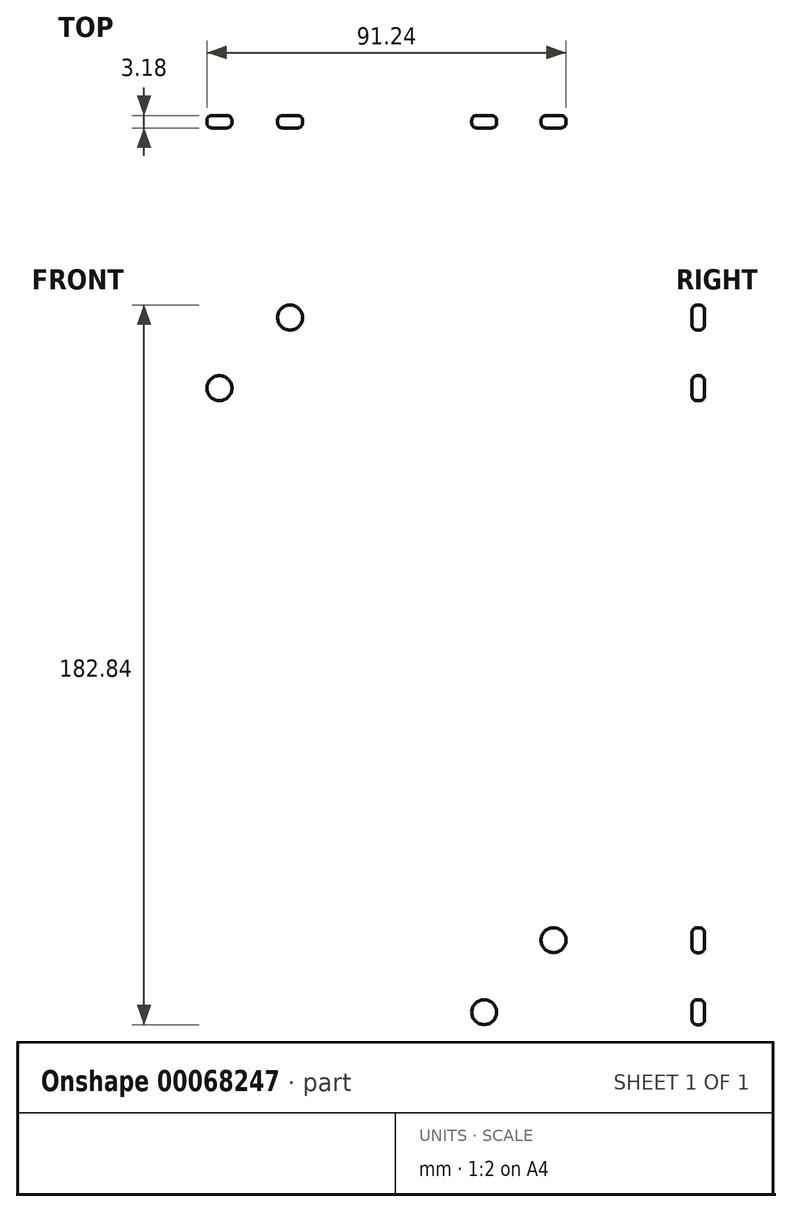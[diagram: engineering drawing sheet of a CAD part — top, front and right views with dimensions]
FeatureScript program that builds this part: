
annotation { "Feature Type Name" : "Feature", "Feature Type Description" : "" }
export const myFeature = defineFeature(function(context is Context, id is Id, definition is map)
    precondition{}
    {
        {
            var Q0;
            Q0=qCreatedBy(makeId("Front.planeOp"),FACE);
            var sketch = newSketch(context, id + "F0", { "sketchPlane" : qUnion([Q0])});
            skLineSegment(sketch, "E0.bottom", {"start": v(-302.85, 118.42) * mm, "end": v(509.95, 118.42) * mm});
            skLineSegment(sketch, "E0.top", {"start": v(-302.85, -103.83) * mm, "end": v(509.95, -103.83) * mm});
            skLineSegment(sketch, "E0.left", {"start": v(-302.85, 118.42) * mm, "end": v(-302.85, -103.83) * mm});
            skLineSegment(sketch, "E0.right", {"start": v(509.95, 118.42) * mm, "end": v(509.95, -103.83) * mm});
            skLineSegment(sketch, "E1", {"start": v(103.55, 118.42) * mm, "end": v(103.55, -103.83) * mm, "construction": true});
            skLineSegment(sketch, "E2", {"start": v(103.55, -103.83) * mm, "end": v(509.95, 7.3) * mm, "construction": true});
            skLineSegment(sketch, "E3", {"start": v(509.95, 7.3) * mm, "end": v(-302.85, 7.3) * mm, "construction": true});
            skLineSegment(sketch, "E4", {"start": v(-302.85, 7.3) * mm, "end": v(103.55, 118.42) * mm, "construction": true});
            skLineSegment(sketch, "E5", {"start": v(509.95, 7.3) * mm, "end": v(103.55, 118.42) * mm, "construction": true});
            skLineSegment(sketch, "E6", {"start": v(-302.85, 7.3) * mm, "end": v(103.55, -103.83) * mm, "construction": true});
            skCircle(sketch, "E7", {"center": v(52.75, 7.3) * mm, "radius": 25.4 * mm});
            skCircle(sketch, "E8", {"center": v(154.35, 7.3) * mm, "radius": 25.4 * mm});
            skLineSegment(sketch, "E9", {"start": v(52.75, 32.7) * mm, "end": v(154.35, 32.7) * mm});
            skLineSegment(sketch, "E10", {"start": v(52.75, -18.1) * mm, "end": v(154.35, -18.1) * mm});
            skLineSegment(sketch, "E11", {"start": v(103.55, 32.7) * mm, "end": v(103.55, 0) * mm, "construction": true});
            skCircle(sketch, "E12", {"center": v(79.74, -60.97) * mm, "radius": 4.76 * mm});
            skCircle(sketch, "E13", {"center": v(127.37, -60.97) * mm, "radius": 4.76 * mm});
            skLineSegment(sketch, "E14", {"start": v(79.74, -56.2) * mm, "end": v(127.37, -56.2) * mm});
            skLineSegment(sketch, "E15", {"start": v(127.37, -65.73) * mm, "end": v(79.74, -65.73) * mm});
            skLineSegment(sketch, "E16", {"start": v(103.55, -78.7) * mm, "end": v(103.55, -62.77) * mm, "construction": true});
            skPoint(sketch, "E16.startSnap0", {"position": v(103.55, -65.73) * mm});
            skLineSegment(sketch, "E17", {"start": v(79.74, 67.62) * mm, "end": v(127.37, 67.62) * mm});
            skLineSegment(sketch, "E18", {"start": v(127.37, 58.1) * mm, "end": v(79.74, 58.1) * mm});
            skCircle(sketch, "E19", {"center": v(127.37, 62.85) * mm, "radius": 4.76 * mm});
            skCircle(sketch, "E20", {"center": v(79.74, 62.85) * mm, "radius": 4.76 * mm});
            skLineSegment(sketch, "E21", {"start": v(103.55, 58.1) * mm, "end": v(103.55, 67.62) * mm, "construction": true});
            skLineSegment(sketch, "E22.1.0.0", {"start": v(19.4, -65.73) * mm, "end": v(-28.22, -65.73) * mm});
            skLineSegment(sketch, "E22.1.0.1", {"start": v(-28.22, -56.2) * mm, "end": v(19.4, -56.2) * mm});
            skCircle(sketch, "E22.1.0.2", {"center": v(19.4, -60.97) * mm, "radius": 4.76 * mm});
            skCircle(sketch, "E22.1.0.3", {"center": v(-28.22, -60.97) * mm, "radius": 4.76 * mm});
            skLineSegment(sketch, "E22.2.0.0", {"start": v(-88.56, -65.73) * mm, "end": v(-136.18, -65.73) * mm});
            skLineSegment(sketch, "E22.2.0.1", {"start": v(-136.18, -56.2) * mm, "end": v(-88.56, -56.2) * mm});
            skCircle(sketch, "E22.2.0.2", {"center": v(-88.56, -60.97) * mm, "radius": 4.76 * mm});
            skCircle(sketch, "E22.2.0.3", {"center": v(-136.18, -60.97) * mm, "radius": 4.76 * mm});
            skLineSegment(sketch, "E22.3.0.0", {"start": v(-196.52, -65.73) * mm, "end": v(-244.14, -65.73) * mm});
            skLineSegment(sketch, "E22.3.0.1", {"start": v(-244.14, -56.2) * mm, "end": v(-196.52, -56.2) * mm});
            skCircle(sketch, "E22.3.0.2", {"center": v(-196.52, -60.97) * mm, "radius": 4.76 * mm});
            skCircle(sketch, "E22.3.0.3", {"center": v(-244.14, -60.97) * mm, "radius": 4.76 * mm});
            skLineSegment(sketch, "E22.direction1", {"start": v(79.74, -65.73) * mm, "end": v(-28.22, -65.73) * mm, "construction": true});
            skCircle(sketch, "E23.1.0.0", {"center": v(19.42, 62.85) * mm, "radius": 4.76 * mm});
            skLineSegment(sketch, "E23.1.0.1", {"start": v(-28.2, 67.62) * mm, "end": v(19.42, 67.62) * mm});
            skCircle(sketch, "E23.1.0.2", {"center": v(-28.2, 62.85) * mm, "radius": 4.76 * mm});
            skLineSegment(sketch, "E23.1.0.3", {"start": v(19.42, 58.1) * mm, "end": v(-28.2, 58.1) * mm});
            skCircle(sketch, "E23.2.0.0", {"center": v(-88.53, 62.85) * mm, "radius": 4.76 * mm});
            skLineSegment(sketch, "E23.2.0.1", {"start": v(-136.16, 67.62) * mm, "end": v(-88.53, 67.62) * mm});
            skCircle(sketch, "E23.2.0.2", {"center": v(-136.16, 62.85) * mm, "radius": 4.76 * mm});
            skLineSegment(sketch, "E23.2.0.3", {"start": v(-88.53, 58.1) * mm, "end": v(-136.16, 58.1) * mm});
            skCircle(sketch, "E23.3.0.0", {"center": v(-196.48, 62.85) * mm, "radius": 4.76 * mm});
            skLineSegment(sketch, "E23.3.0.1", {"start": v(-244.1, 67.62) * mm, "end": v(-196.48, 67.62) * mm});
            skCircle(sketch, "E23.3.0.2", {"center": v(-244.1, 62.85) * mm, "radius": 4.76 * mm});
            skLineSegment(sketch, "E23.3.0.3", {"start": v(-196.48, 58.1) * mm, "end": v(-244.1, 58.1) * mm});
            skLineSegment(sketch, "E23.direction1", {"start": v(127.37, 62.85) * mm, "end": v(19.42, 62.85) * mm, "construction": true});
            skCircle(sketch, "E24.MirrorC", {"center": v(187.7, 62.85) * mm, "radius": 4.76 * mm});
            skLineSegment(sketch, "E25.MirrorCS", {"start": v(187.7, 58.1) * mm, "end": v(235.32, 58.1) * mm});
            skCircle(sketch, "E26.MirrorC", {"center": v(235.32, 62.85) * mm, "radius": 4.76 * mm});
            skLineSegment(sketch, "E27.MirrorCS", {"start": v(235.32, 67.62) * mm, "end": v(187.7, 67.62) * mm});
            skCircle(sketch, "E28.MirrorC", {"center": v(295.64, 62.85) * mm, "radius": 4.76 * mm});
            skLineSegment(sketch, "E29.MirrorCS", {"start": v(343.27, 67.62) * mm, "end": v(295.64, 67.62) * mm});
            skLineSegment(sketch, "E30.MirrorCS", {"start": v(295.64, 58.1) * mm, "end": v(343.27, 58.1) * mm});
            skCircle(sketch, "E31.MirrorC", {"center": v(343.27, 62.85) * mm, "radius": 4.76 * mm});
            skCircle(sketch, "E32.MirrorC", {"center": v(451.22, 62.85) * mm, "radius": 4.76 * mm});
            skCircle(sketch, "E33.MirrorC", {"center": v(403.6, 62.85) * mm, "radius": 4.76 * mm});
            skLineSegment(sketch, "E34.MirrorCS", {"start": v(403.6, 58.1) * mm, "end": v(451.22, 58.1) * mm});
            skLineSegment(sketch, "E35.MirrorCS", {"start": v(451.22, 67.62) * mm, "end": v(403.6, 67.62) * mm});
            skCircle(sketch, "E36.MirrorC", {"center": v(451.25, -60.97) * mm, "radius": 4.76 * mm});
            skCircle(sketch, "E37.MirrorC", {"center": v(403.63, -60.97) * mm, "radius": 4.76 * mm});
            skLineSegment(sketch, "E38.MirrorCS", {"start": v(451.25, -56.2) * mm, "end": v(403.63, -56.2) * mm});
            skLineSegment(sketch, "E39.MirrorCS", {"start": v(403.63, -65.73) * mm, "end": v(451.25, -65.73) * mm});
            skCircle(sketch, "E40.MirrorC", {"center": v(343.29, -60.97) * mm, "radius": 4.76 * mm});
            skCircle(sketch, "E41.MirrorC", {"center": v(295.66, -60.97) * mm, "radius": 4.76 * mm});
            skLineSegment(sketch, "E42.MirrorCS", {"start": v(343.29, -56.2) * mm, "end": v(295.66, -56.2) * mm});
            skLineSegment(sketch, "E43.MirrorCS", {"start": v(295.66, -65.73) * mm, "end": v(343.29, -65.73) * mm});
            skLineSegment(sketch, "E44.MirrorCS", {"start": v(235.33, -56.2) * mm, "end": v(187.7, -56.2) * mm});
            skLineSegment(sketch, "E45.MirrorCS", {"start": v(187.7, -65.73) * mm, "end": v(235.33, -65.73) * mm});
            skCircle(sketch, "E46.MirrorC", {"center": v(187.7, -60.97) * mm, "radius": 4.76 * mm});
            skCircle(sketch, "E47.MirrorC", {"center": v(235.33, -60.97) * mm, "radius": 4.76 * mm});
            skLineSegment(sketch, "E48", {"start": v(509.95, 62.85) * mm, "end": v(-302.85, 62.85) * mm, "construction": true});
            skLineSegment(sketch, "E49", {"start": v(-302.85, -60.97) * mm, "end": v(509.95, -60.97) * mm, "construction": true});
            skCircle(sketch, "E50", {"center": v(-294.9, -60.97) * mm, "radius": 4.76 * mm});
            skCircle(sketch, "E51", {"center": v(-272.68, -60.97) * mm, "radius": 4.76 * mm});
            skLineSegment(sketch, "E52", {"start": v(-294.9, -56.2) * mm, "end": v(-272.68, -56.2) * mm});
            skLineSegment(sketch, "E53", {"start": v(-294.9, -65.73) * mm, "end": v(-272.68, -65.73) * mm});
            skLineSegment(sketch, "E54", {"start": v(-293.9, 67.62) * mm, "end": v(-271.67, 67.62) * mm});
            skCircle(sketch, "E55", {"center": v(-293.9, 62.85) * mm, "radius": 4.76 * mm});
            skCircle(sketch, "E56", {"center": v(-271.67, 62.85) * mm, "radius": 4.76 * mm});
            skLineSegment(sketch, "E57", {"start": v(-293.9, 58.1) * mm, "end": v(-271.67, 58.1) * mm});
            skLineSegment(sketch, "E58", {"start": v(-293.9, 62.85) * mm, "end": v(-271.67, 62.85) * mm, "construction": true});
            skLineSegment(sketch, "E59", {"start": v(-293.9, 67.62) * mm, "end": v(-294.9, -65.73) * mm, "construction": true});
            skCircle(sketch, "E60.MirrorC", {"center": v(478.78, 62.85) * mm, "radius": 4.76 * mm});
            skLineSegment(sketch, "E61.MirrorCS", {"start": v(501, 67.62) * mm, "end": v(478.78, 67.62) * mm});
            skLineSegment(sketch, "E62.MirrorCS", {"start": v(501, 58.1) * mm, "end": v(478.78, 58.1) * mm});
            skCircle(sketch, "E63.MirrorC", {"center": v(501, 62.85) * mm, "radius": 4.76 * mm});
            skLineSegment(sketch, "E64.MirrorCS", {"start": v(502.02, -56.2) * mm, "end": v(479.8, -56.2) * mm});
            skCircle(sketch, "E65.MirrorC", {"center": v(502.02, -60.97) * mm, "radius": 4.76 * mm});
            skLineSegment(sketch, "E66.MirrorCS", {"start": v(502.02, -65.73) * mm, "end": v(479.8, -65.73) * mm});
            skCircle(sketch, "E67.MirrorC", {"center": v(479.8, -60.97) * mm, "radius": 4.76 * mm});
            skLineSegment(sketch, "E68", {"start": v(-302.85, -103.83) * mm, "end": v(509.95, 118.42) * mm, "construction": true});
            skLineSegment(sketch, "E69", {"start": v(509.95, -103.83) * mm, "end": v(-302.85, 118.42) * mm, "construction": true});
            skSolve(sketch);
        }
        {
            var Q0;
            Q0=makeQuery(id+"F0.imprint","IMPRINT",FACE,{"disambiguationData":[TD([[makeQuery(id+"F0.imprint","IMPRINT",EDGE,{"derivedFrom":sQuery(id+"F0.wireOp",EDGE,"E0.bottom")}),-1.0]])]});
            extrude(context, id + "F1", {"entities" : qUnion([Q0]), "depth" : 9.52 * mm});
        }
        {
            var Q0;
            Q0=makeQuery(id+"F1.opExtrude","SWEPT_FACE",FACE,{"disambiguationData":[OSD([sQuery(id+"F0.wireOp",EDGE,"E0.left")])]});
            var sketch = newSketch(context, id + "F2", { "sketchPlane" : qUnion([Q0])});
            skLineSegment(sketch, "E70.0", {"start": v(9.53, 118.42) * mm, "end": v(0, 118.42) * mm});
            skLineSegment(sketch, "E70.1", {"start": v(9.53, 118.42) * mm, "end": v(9.53, -103.83) * mm});
            skLineSegment(sketch, "E70.2", {"start": v(0, 118.42) * mm, "end": v(0, -103.83) * mm});
            skLineSegment(sketch, "E70.3", {"start": v(9.53, -103.83) * mm, "end": v(0, -103.83) * mm});
            skLineSegment(sketch, "E71.bottom", {"start": v(0, 118.42) * mm, "end": v(6.35, 118.42) * mm});
            skLineSegment(sketch, "E71.top", {"start": v(0, 112.07) * mm, "end": v(6.35, 112.07) * mm});
            skLineSegment(sketch, "E71.left", {"start": v(0, 118.42) * mm, "end": v(0, 112.07) * mm});
            skLineSegment(sketch, "E71.right", {"start": v(6.35, 118.42) * mm, "end": v(6.35, 112.07) * mm});
            skLineSegment(sketch, "E72.bottom", {"start": v(6.35, -103.83) * mm, "end": v(3.18, -103.83) * mm});
            skLineSegment(sketch, "E72.top", {"start": v(6.35, -100.66) * mm, "end": v(3.18, -100.66) * mm});
            skLineSegment(sketch, "E72.left", {"start": v(6.35, -103.83) * mm, "end": v(6.35, -100.66) * mm});
            skLineSegment(sketch, "E72.right", {"start": v(3.18, -103.83) * mm, "end": v(3.18, -100.66) * mm});
            skLineSegment(sketch, "E73.bottom", {"start": v(9.52, 108.9) * mm, "end": v(3.17, 108.9) * mm});
            skLineSegment(sketch, "E73.top", {"start": v(9.53, -94.3) * mm, "end": v(3.18, -94.3) * mm});
            skLineSegment(sketch, "E73.left", {"start": v(9.52, 108.9) * mm, "end": v(9.53, -94.3) * mm});
            skLineSegment(sketch, "E73.right", {"start": v(3.17, 108.9) * mm, "end": v(3.18, -94.3) * mm});
            skLineSegment(sketch, "E74", {"start": v(3.18, -100.66) * mm, "end": v(3.18, -94.3) * mm});
            skLineSegment(sketch, "E75", {"start": v(6.35, -100.66) * mm, "end": v(6.35, -94.3) * mm});
            skSolve(sketch);
        }
        {
            var Q0;
            Q0=makeQuery(id+"F2.imprint","IMPRINT",FACE,{"disambiguationData":[TD([[makeQuery(id+"F2.imprint","IMPRINT",EDGE,{"derivedFrom":sQuery(id+"F2.wireOp",EDGE,"E72.top")}),-1.0]])]});
            var Q1;
            Q1=makeQuery(id+"F2.imprint","IMPRINT",FACE,{"disambiguationData":[TD([[makeQuery(id+"F2.imprint","IMPRINT",EDGE,{"derivedFrom":sQuery(id+"F2.wireOp",EDGE,"E73.bottom")}),1.0]])]});
            var Q2;
            Q2=makeQuery(id+"F2.imprint","IMPRINT",FACE,{"disambiguationData":[TD([[makeQuery(id+"F2.imprint","IMPRINT",EDGE,{"derivedFrom":sQuery(id+"F2.wireOp",EDGE,"E71.bottom")}),1.0]])]});
            extrude(context, id + "F3", {"entities" : qUnion([Q0, Q1, Q2]), "operationType" : NewBodyOperationType.REMOVE, "endBound" : BoundingType.THROUGH_ALL, "oppositeDirection" : true, "depth" : 25.4 * mm});
        }
        {
            var Q0;
            Q0=makeQuery(id+"F1.opExtrude","CAP_FACE",FACE,{"disambiguationData":[OSD([sQuery(id+"F0.wireOp",EDGE,"E0.bottom"),sQuery(id+"F0.wireOp",EDGE,"E0.top"),sQuery(id+"F0.wireOp",EDGE,"E0.left"),sQuery(id+"F0.wireOp",EDGE,"E0.right"),sQuery(id+"F0.wireOp",EDGE,"E7"),sQuery(id+"F0.wireOp",EDGE,"E8"),sQuery(id+"F0.wireOp",EDGE,"E9"),sQuery(id+"F0.wireOp",EDGE,"E10"),sQuery(id+"F0.wireOp",EDGE,"E12"),sQuery(id+"F0.wireOp",EDGE,"E13"),sQuery(id+"F0.wireOp",EDGE,"E14"),sQuery(id+"F0.wireOp",EDGE,"E15"),sQuery(id+"F0.wireOp",EDGE,"E17"),sQuery(id+"F0.wireOp",EDGE,"E18"),sQuery(id+"F0.wireOp",EDGE,"E19"),sQuery(id+"F0.wireOp",EDGE,"E20"),sQuery(id+"F0.wireOp",EDGE,"E22.1.0.0"),sQuery(id+"F0.wireOp",EDGE,"E22.1.0.1"),sQuery(id+"F0.wireOp",EDGE,"E22.1.0.2"),sQuery(id+"F0.wireOp",EDGE,"E22.1.0.3"),sQuery(id+"F0.wireOp",EDGE,"E22.2.0.0"),sQuery(id+"F0.wireOp",EDGE,"E22.2.0.1"),sQuery(id+"F0.wireOp",EDGE,"E22.2.0.2"),sQuery(id+"F0.wireOp",EDGE,"E22.2.0.3"),sQuery(id+"F0.wireOp",EDGE,"E22.3.0.0"),sQuery(id+"F0.wireOp",EDGE,"E22.3.0.1"),sQuery(id+"F0.wireOp",EDGE,"E22.3.0.2"),sQuery(id+"F0.wireOp",EDGE,"E22.3.0.3"),sQuery(id+"F0.wireOp",EDGE,"E23.1.0.0"),sQuery(id+"F0.wireOp",EDGE,"E23.1.0.1"),sQuery(id+"F0.wireOp",EDGE,"E23.1.0.2"),sQuery(id+"F0.wireOp",EDGE,"E23.1.0.3"),sQuery(id+"F0.wireOp",EDGE,"E23.2.0.0"),sQuery(id+"F0.wireOp",EDGE,"E23.2.0.1"),sQuery(id+"F0.wireOp",EDGE,"E23.2.0.2"),sQuery(id+"F0.wireOp",EDGE,"E23.2.0.3"),sQuery(id+"F0.wireOp",EDGE,"E23.3.0.0"),sQuery(id+"F0.wireOp",EDGE,"E23.3.0.1"),sQuery(id+"F0.wireOp",EDGE,"E23.3.0.2"),sQuery(id+"F0.wireOp",EDGE,"E23.3.0.3"),sQuery(id+"F0.wireOp",EDGE,"E24.MirrorC"),sQuery(id+"F0.wireOp",EDGE,"E25.MirrorCS"),sQuery(id+"F0.wireOp",EDGE,"E26.MirrorC"),sQuery(id+"F0.wireOp",EDGE,"E27.MirrorCS"),sQuery(id+"F0.wireOp",EDGE,"E28.MirrorC"),sQuery(id+"F0.wireOp",EDGE,"E29.MirrorCS"),sQuery(id+"F0.wireOp",EDGE,"E30.MirrorCS"),sQuery(id+"F0.wireOp",EDGE,"E31.MirrorC"),sQuery(id+"F0.wireOp",EDGE,"E32.MirrorC"),sQuery(id+"F0.wireOp",EDGE,"E33.MirrorC"),sQuery(id+"F0.wireOp",EDGE,"E34.MirrorCS"),sQuery(id+"F0.wireOp",EDGE,"E35.MirrorCS"),sQuery(id+"F0.wireOp",EDGE,"E36.MirrorC"),sQuery(id+"F0.wireOp",EDGE,"E37.MirrorC"),sQuery(id+"F0.wireOp",EDGE,"E38.MirrorCS"),sQuery(id+"F0.wireOp",EDGE,"E39.MirrorCS"),sQuery(id+"F0.wireOp",EDGE,"E40.MirrorC"),sQuery(id+"F0.wireOp",EDGE,"E41.MirrorC"),sQuery(id+"F0.wireOp",EDGE,"E42.MirrorCS"),sQuery(id+"F0.wireOp",EDGE,"E43.MirrorCS"),sQuery(id+"F0.wireOp",EDGE,"E44.MirrorCS"),sQuery(id+"F0.wireOp",EDGE,"E45.MirrorCS"),sQuery(id+"F0.wireOp",EDGE,"E46.MirrorC"),sQuery(id+"F0.wireOp",EDGE,"E47.MirrorC"),sQuery(id+"F0.wireOp",EDGE,"E50"),sQuery(id+"F0.wireOp",EDGE,"E51"),sQuery(id+"F0.wireOp",EDGE,"E52"),sQuery(id+"F0.wireOp",EDGE,"E53"),sQuery(id+"F0.wireOp",EDGE,"E54"),sQuery(id+"F0.wireOp",EDGE,"E55"),sQuery(id+"F0.wireOp",EDGE,"E56"),sQuery(id+"F0.wireOp",EDGE,"E57"),sQuery(id+"F0.wireOp",EDGE,"E60.MirrorC"),sQuery(id+"F0.wireOp",EDGE,"E61.MirrorCS"),sQuery(id+"F0.wireOp",EDGE,"E62.MirrorCS"),sQuery(id+"F0.wireOp",EDGE,"E63.MirrorC"),sQuery(id+"F0.wireOp",EDGE,"E64.MirrorCS"),sQuery(id+"F0.wireOp",EDGE,"E65.MirrorC"),sQuery(id+"F0.wireOp",EDGE,"E66.MirrorCS"),sQuery(id+"F0.wireOp",EDGE,"E67.MirrorC")])],"isStart":true});
            var sketch = newSketch(context, id + "F4", { "sketchPlane" : qUnion([Q0])});
            skLineSegment(sketch, "E76.0", {"start": v(301.58, 110.8) * mm, "end": v(-508.68, 110.8) * mm});
            skLineSegment(sketch, "E76.1", {"start": v(-508.68, -102.56) * mm, "end": v(301.58, -102.56) * mm});
            skLineSegment(sketch, "E76.2", {"start": v(-508.68, 110.8) * mm, "end": v(-508.68, -102.56) * mm});
            skLineSegment(sketch, "E76.3", {"start": v(302.85, 110.8) * mm, "end": v(302.85, -102.56) * mm});
            skLineSegment(sketch, "E77", {"start": v(-103.55, 110.8) * mm, "end": v(-103.55, -102.56) * mm, "construction": true});
            skCircle(sketch, "E78", {"center": v(-127.37, 88.25) * mm, "radius": 3.18 * mm});
            skArc(sketch, "E79.0", {"start": v(-127.37, 56.82) * mm, "mid": v(-133.4, 62.85) * mm, "end": v(-127.37, 68.89) * mm});
            skArc(sketch, "E79.1", {"start": v(-127.37, -67) * mm, "mid": v(-133.4, -60.97) * mm, "end": v(-127.37, -54.94) * mm});
            skCircle(sketch, "E80", {"center": v(-145.33, 70.3) * mm, "radius": 3.18 * mm});
            skLineSegment(sketch, "E81", {"start": v(-129.61, 90.5) * mm, "end": v(-147.57, 72.54) * mm});
            skLineSegment(sketch, "E82", {"start": v(-125.12, 86) * mm, "end": v(-143.08, 68.05) * mm});
            skLineSegment(sketch, "E83", {"start": v(-127.37, 88.25) * mm, "end": v(-161.51, 88.25) * mm, "construction": true});
            skLineSegment(sketch, "E84", {"start": v(-127.37, 88.25) * mm, "end": v(-127.37, 62.85) * mm, "construction": true});
            skLineSegment(sketch, "E85", {"start": v(-127.37, 88.25) * mm, "end": v(-145.33, 70.3) * mm, "construction": true});
            skLineSegment(sketch, "E86", {"start": v(-127.37, 62.85) * mm, "end": v(-127.37, -60.97) * mm, "construction": true});
            skLineSegment(sketch, "E87", {"start": v(-127.37, 0) * mm, "end": v(-225.54, 0.94) * mm, "construction": true});
            skPoint(sketch, "E87.startSnap0", {"position": v(-127.37, 0.94) * mm});
            skPoint(sketch, "E87.endSnap0", {"position": v(-127.37, 0.94) * mm});
            skLineSegment(sketch, "E88.MirrorCS", {"start": v(-126.77, -86.04) * mm, "end": v(-144.38, -67.73) * mm});
            skLineSegment(sketch, "E89.MirrorCS", {"start": v(-131.35, -90.44) * mm, "end": v(-148.96, -72.14) * mm});
            skCircle(sketch, "E90.MirrorC", {"center": v(-129.06, -88.24) * mm, "radius": 3.18 * mm});
            skCircle(sketch, "E91.MirrorC", {"center": v(-146.67, -69.94) * mm, "radius": 3.18 * mm});
            skCircle(sketch, "E92.MirrorC", {"center": v(-79.74, 88.25) * mm, "radius": 3.18 * mm});
            skLineSegment(sketch, "E93.MirrorCS", {"start": v(-77.5, 90.5) * mm, "end": v(-59.54, 72.54) * mm});
            skLineSegment(sketch, "E94.MirrorCS", {"start": v(-81.99, 86) * mm, "end": v(-64.03, 68.05) * mm});
            skCircle(sketch, "E95.MirrorC", {"center": v(-61.78, 70.3) * mm, "radius": 3.18 * mm});
            skLineSegment(sketch, "E96.MirrorCS", {"start": v(-75.76, -90.44) * mm, "end": v(-58.15, -72.14) * mm});
            skLineSegment(sketch, "E97.MirrorCS", {"start": v(-80.34, -86.04) * mm, "end": v(-62.73, -67.73) * mm});
            skCircle(sketch, "E98.MirrorC", {"center": v(-60.44, -69.94) * mm, "radius": 3.18 * mm});
            skCircle(sketch, "E99.MirrorC", {"center": v(-78.05, -88.24) * mm, "radius": 3.18 * mm});
            skSolve(sketch);
        }
        {
            var Q0;
            {var subQ0=sQuery(id+"F4.wireOp",EDGE,"E78");var subQ1=makeQuery(id+"F4.imprint","INTERSECT",VERTEX,{"derivedFrom":[subQ0,sQuery(id+"F4.wireOp",EDGE,"E81")]});Q0=makeQuery(id+"F4.imprint","IMPRINT",FACE,{"disambiguationData":[TD([[makeQuery(id+"F4.imprint","IMPRINT",EDGE,{"disambiguationData":[TD([[subQ1,-1.0]])],"derivedFrom":subQ0}),1.0]])]});}
            var Q1;
            {var subQ0=sQuery(id+"F4.wireOp",EDGE,"E81");Q1=makeQuery(id+"F4.imprint","IMPRINT",FACE,{"disambiguationData":[TD([[makeQuery(id+"F4.imprint","IMPRINT",EDGE,{"derivedFrom":subQ0}),1.0]])]});}
            var Q2;
            {var subQ0=sQuery(id+"F4.wireOp",EDGE,"E80");var subQ1=makeQuery(id+"F4.imprint","INTERSECT",VERTEX,{"derivedFrom":[subQ0,sQuery(id+"F4.wireOp",EDGE,"E81")]});Q2=makeQuery(id+"F4.imprint","IMPRINT",FACE,{"disambiguationData":[TD([[makeQuery(id+"F4.imprint","IMPRINT",EDGE,{"disambiguationData":[TD([[subQ1,-1.0]])],"derivedFrom":subQ0}),1.0]])]});}
            var Q3;
            {var subQ0=sQuery(id+"F4.wireOp",EDGE,"E92.MirrorC");var subQ1=makeQuery(id+"F4.imprint","INTERSECT",VERTEX,{"derivedFrom":[subQ0,sQuery(id+"F4.wireOp",EDGE,"E93.MirrorCS")]});Q3=makeQuery(id+"F4.imprint","IMPRINT",FACE,{"disambiguationData":[TD([[makeQuery(id+"F4.imprint","IMPRINT",EDGE,{"disambiguationData":[TD([[subQ1,-1.0]])],"derivedFrom":subQ0}),-1.0]])]});}
            var Q4;
            {var subQ0=sQuery(id+"F4.wireOp",EDGE,"E93.MirrorCS");Q4=makeQuery(id+"F4.imprint","IMPRINT",FACE,{"disambiguationData":[TD([[makeQuery(id+"F4.imprint","IMPRINT",EDGE,{"derivedFrom":subQ0}),-1.0]])]});}
            var Q5;
            {var subQ0=sQuery(id+"F4.wireOp",EDGE,"E95.MirrorC");var subQ1=makeQuery(id+"F4.imprint","INTERSECT",VERTEX,{"derivedFrom":[sQuery(id+"F4.wireOp",EDGE,"E93.MirrorCS"),subQ0]});Q5=makeQuery(id+"F4.imprint","IMPRINT",FACE,{"disambiguationData":[TD([[makeQuery(id+"F4.imprint","IMPRINT",EDGE,{"disambiguationData":[TD([[subQ1,-1.0]])],"derivedFrom":subQ0}),-1.0]])]});}
            var Q6;
            {var subQ0=sQuery(id+"F4.wireOp",EDGE,"E91.MirrorC");var subQ1=makeQuery(id+"F4.imprint","INTERSECT",VERTEX,{"derivedFrom":[sQuery(id+"F4.wireOp",EDGE,"E88.MirrorCS"),subQ0]});Q6=makeQuery(id+"F4.imprint","IMPRINT",FACE,{"disambiguationData":[TD([[makeQuery(id+"F4.imprint","IMPRINT",EDGE,{"disambiguationData":[TD([[subQ1,1.0]])],"derivedFrom":subQ0}),-1.0]])]});}
            var Q7;
            {var subQ0=sQuery(id+"F4.wireOp",EDGE,"E88.MirrorCS");Q7=makeQuery(id+"F4.imprint","IMPRINT",FACE,{"disambiguationData":[TD([[makeQuery(id+"F4.imprint","IMPRINT",EDGE,{"derivedFrom":subQ0}),1.0]])]});}
            var Q8;
            {var subQ0=sQuery(id+"F4.wireOp",EDGE,"E90.MirrorC");var subQ1=makeQuery(id+"F4.imprint","INTERSECT",VERTEX,{"derivedFrom":[sQuery(id+"F4.wireOp",EDGE,"E88.MirrorCS"),subQ0]});Q8=makeQuery(id+"F4.imprint","IMPRINT",FACE,{"disambiguationData":[TD([[makeQuery(id+"F4.imprint","IMPRINT",EDGE,{"disambiguationData":[TD([[subQ1,1.0]])],"derivedFrom":subQ0}),-1.0]])]});}
            var Q9;
            {var subQ0=sQuery(id+"F4.wireOp",EDGE,"E99.MirrorC");var subQ1=makeQuery(id+"F4.imprint","INTERSECT",VERTEX,{"derivedFrom":[sQuery(id+"F4.wireOp",EDGE,"E96.MirrorCS"),subQ0]});Q9=makeQuery(id+"F4.imprint","IMPRINT",FACE,{"disambiguationData":[TD([[makeQuery(id+"F4.imprint","IMPRINT",EDGE,{"disambiguationData":[TD([[subQ1,-1.0]])],"derivedFrom":subQ0}),1.0]])]});}
            var Q10;
            {var subQ0=sQuery(id+"F4.wireOp",EDGE,"E96.MirrorCS");Q10=makeQuery(id+"F4.imprint","IMPRINT",FACE,{"disambiguationData":[TD([[makeQuery(id+"F4.imprint","IMPRINT",EDGE,{"derivedFrom":subQ0}),1.0]])]});}
            var Q11;
            {var subQ0=sQuery(id+"F4.wireOp",EDGE,"E98.MirrorC");var subQ1=makeQuery(id+"F4.imprint","INTERSECT",VERTEX,{"derivedFrom":[sQuery(id+"F4.wireOp",EDGE,"E96.MirrorCS"),subQ0]});Q11=makeQuery(id+"F4.imprint","IMPRINT",FACE,{"disambiguationData":[TD([[makeQuery(id+"F4.imprint","IMPRINT",EDGE,{"disambiguationData":[TD([[subQ1,-1.0]])],"derivedFrom":subQ0}),1.0]])]});}
            extrude(context, id + "F5", {"entities" : qUnion([Q0, Q1, Q2, Q3, Q4, Q5, Q6, Q7, Q8, Q9, Q10, Q11]), "operationType" : NewBodyOperationType.REMOVE, "endBound" : BoundingType.THROUGH_ALL, "oppositeDirection" : true, "depth" : 25.4 * mm});
        }
        {
            var Q0;
            Q0=makeQuery(id+"F3.boolean.opBoolean","COPY",FACE,{"derivedFrom":makeQuery(id+"F3.opExtrude","SWEPT_FACE",FACE,{"disambiguationData":[OSD([sQuery(id+"F2.wireOp",EDGE,"E73.right"),sQuery(id+"F2.wireOp",EDGE,"E74")])]})});
            var Q1;
            Q1=makeQuery(id+"F1.opExtrude","CAP_FACE",FACE,{"disambiguationData":[OSD([sQuery(id+"F0.wireOp",EDGE,"E0.bottom"),sQuery(id+"F0.wireOp",EDGE,"E0.top"),sQuery(id+"F0.wireOp",EDGE,"E0.left"),sQuery(id+"F0.wireOp",EDGE,"E0.right"),sQuery(id+"F0.wireOp",EDGE,"E7"),sQuery(id+"F0.wireOp",EDGE,"E8"),sQuery(id+"F0.wireOp",EDGE,"E9"),sQuery(id+"F0.wireOp",EDGE,"E10"),sQuery(id+"F0.wireOp",EDGE,"E12"),sQuery(id+"F0.wireOp",EDGE,"E13"),sQuery(id+"F0.wireOp",EDGE,"E14"),sQuery(id+"F0.wireOp",EDGE,"E15"),sQuery(id+"F0.wireOp",EDGE,"E17"),sQuery(id+"F0.wireOp",EDGE,"E18"),sQuery(id+"F0.wireOp",EDGE,"E19"),sQuery(id+"F0.wireOp",EDGE,"E20"),sQuery(id+"F0.wireOp",EDGE,"E22.1.0.0"),sQuery(id+"F0.wireOp",EDGE,"E22.1.0.1"),sQuery(id+"F0.wireOp",EDGE,"E22.1.0.2"),sQuery(id+"F0.wireOp",EDGE,"E22.1.0.3"),sQuery(id+"F0.wireOp",EDGE,"E22.2.0.0"),sQuery(id+"F0.wireOp",EDGE,"E22.2.0.1"),sQuery(id+"F0.wireOp",EDGE,"E22.2.0.2"),sQuery(id+"F0.wireOp",EDGE,"E22.2.0.3"),sQuery(id+"F0.wireOp",EDGE,"E22.3.0.0"),sQuery(id+"F0.wireOp",EDGE,"E22.3.0.1"),sQuery(id+"F0.wireOp",EDGE,"E22.3.0.2"),sQuery(id+"F0.wireOp",EDGE,"E22.3.0.3"),sQuery(id+"F0.wireOp",EDGE,"E23.1.0.0"),sQuery(id+"F0.wireOp",EDGE,"E23.1.0.1"),sQuery(id+"F0.wireOp",EDGE,"E23.1.0.2"),sQuery(id+"F0.wireOp",EDGE,"E23.1.0.3"),sQuery(id+"F0.wireOp",EDGE,"E23.2.0.0"),sQuery(id+"F0.wireOp",EDGE,"E23.2.0.1"),sQuery(id+"F0.wireOp",EDGE,"E23.2.0.2"),sQuery(id+"F0.wireOp",EDGE,"E23.2.0.3"),sQuery(id+"F0.wireOp",EDGE,"E23.3.0.0"),sQuery(id+"F0.wireOp",EDGE,"E23.3.0.1"),sQuery(id+"F0.wireOp",EDGE,"E23.3.0.2"),sQuery(id+"F0.wireOp",EDGE,"E23.3.0.3"),sQuery(id+"F0.wireOp",EDGE,"E24.MirrorC"),sQuery(id+"F0.wireOp",EDGE,"E25.MirrorCS"),sQuery(id+"F0.wireOp",EDGE,"E26.MirrorC"),sQuery(id+"F0.wireOp",EDGE,"E27.MirrorCS"),sQuery(id+"F0.wireOp",EDGE,"E28.MirrorC"),sQuery(id+"F0.wireOp",EDGE,"E29.MirrorCS"),sQuery(id+"F0.wireOp",EDGE,"E30.MirrorCS"),sQuery(id+"F0.wireOp",EDGE,"E31.MirrorC"),sQuery(id+"F0.wireOp",EDGE,"E32.MirrorC"),sQuery(id+"F0.wireOp",EDGE,"E33.MirrorC"),sQuery(id+"F0.wireOp",EDGE,"E34.MirrorCS"),sQuery(id+"F0.wireOp",EDGE,"E35.MirrorCS"),sQuery(id+"F0.wireOp",EDGE,"E36.MirrorC"),sQuery(id+"F0.wireOp",EDGE,"E37.MirrorC"),sQuery(id+"F0.wireOp",EDGE,"E38.MirrorCS"),sQuery(id+"F0.wireOp",EDGE,"E39.MirrorCS"),sQuery(id+"F0.wireOp",EDGE,"E40.MirrorC"),sQuery(id+"F0.wireOp",EDGE,"E41.MirrorC"),sQuery(id+"F0.wireOp",EDGE,"E42.MirrorCS"),sQuery(id+"F0.wireOp",EDGE,"E43.MirrorCS"),sQuery(id+"F0.wireOp",EDGE,"E44.MirrorCS"),sQuery(id+"F0.wireOp",EDGE,"E45.MirrorCS"),sQuery(id+"F0.wireOp",EDGE,"E46.MirrorC"),sQuery(id+"F0.wireOp",EDGE,"E47.MirrorC"),sQuery(id+"F0.wireOp",EDGE,"E50"),sQuery(id+"F0.wireOp",EDGE,"E51"),sQuery(id+"F0.wireOp",EDGE,"E52"),sQuery(id+"F0.wireOp",EDGE,"E53"),sQuery(id+"F0.wireOp",EDGE,"E54"),sQuery(id+"F0.wireOp",EDGE,"E55"),sQuery(id+"F0.wireOp",EDGE,"E56"),sQuery(id+"F0.wireOp",EDGE,"E57"),sQuery(id+"F0.wireOp",EDGE,"E60.MirrorC"),sQuery(id+"F0.wireOp",EDGE,"E61.MirrorCS"),sQuery(id+"F0.wireOp",EDGE,"E62.MirrorCS"),sQuery(id+"F0.wireOp",EDGE,"E63.MirrorC"),sQuery(id+"F0.wireOp",EDGE,"E64.MirrorCS"),sQuery(id+"F0.wireOp",EDGE,"E65.MirrorC"),sQuery(id+"F0.wireOp",EDGE,"E66.MirrorCS"),sQuery(id+"F0.wireOp",EDGE,"E67.MirrorC")])],"isStart":true});
            var Q2;
            {var subQ0=sQuery(id+"F0.wireOp",EDGE,"E0.bottom");var subQ1=sQuery(id+"F0.wireOp",EDGE,"E0.left");var subQ2=sQuery(id+"F0.wireOp",EDGE,"E0.right");Q2=makeQuery(id+"F3.boolean.opBoolean","SPLIT",FACE,{"disambiguationData":[TD([makeQuery(id+"F1.opExtrude","SWEPT_FACE",FACE,{"disambiguationData":[OSD([subQ0])]})])],"derivedFrom":makeQuery(id+"F1.opExtrude","CAP_FACE",FACE,{"disambiguationData":[OSD([subQ0,sQuery(id+"F0.wireOp",EDGE,"E0.top"),subQ1,subQ2,sQuery(id+"F0.wireOp",EDGE,"E7"),sQuery(id+"F0.wireOp",EDGE,"E8"),sQuery(id+"F0.wireOp",EDGE,"E9"),sQuery(id+"F0.wireOp",EDGE,"E10"),sQuery(id+"F0.wireOp",EDGE,"E12"),sQuery(id+"F0.wireOp",EDGE,"E13"),sQuery(id+"F0.wireOp",EDGE,"E14"),sQuery(id+"F0.wireOp",EDGE,"E15"),sQuery(id+"F0.wireOp",EDGE,"E17"),sQuery(id+"F0.wireOp",EDGE,"E18"),sQuery(id+"F0.wireOp",EDGE,"E19"),sQuery(id+"F0.wireOp",EDGE,"E20"),sQuery(id+"F0.wireOp",EDGE,"E22.1.0.0"),sQuery(id+"F0.wireOp",EDGE,"E22.1.0.1"),sQuery(id+"F0.wireOp",EDGE,"E22.1.0.2"),sQuery(id+"F0.wireOp",EDGE,"E22.1.0.3"),sQuery(id+"F0.wireOp",EDGE,"E22.2.0.0"),sQuery(id+"F0.wireOp",EDGE,"E22.2.0.1"),sQuery(id+"F0.wireOp",EDGE,"E22.2.0.2"),sQuery(id+"F0.wireOp",EDGE,"E22.2.0.3"),sQuery(id+"F0.wireOp",EDGE,"E22.3.0.0"),sQuery(id+"F0.wireOp",EDGE,"E22.3.0.1"),sQuery(id+"F0.wireOp",EDGE,"E22.3.0.2"),sQuery(id+"F0.wireOp",EDGE,"E22.3.0.3"),sQuery(id+"F0.wireOp",EDGE,"E23.1.0.0"),sQuery(id+"F0.wireOp",EDGE,"E23.1.0.1"),sQuery(id+"F0.wireOp",EDGE,"E23.1.0.2"),sQuery(id+"F0.wireOp",EDGE,"E23.1.0.3"),sQuery(id+"F0.wireOp",EDGE,"E23.2.0.0"),sQuery(id+"F0.wireOp",EDGE,"E23.2.0.1"),sQuery(id+"F0.wireOp",EDGE,"E23.2.0.2"),sQuery(id+"F0.wireOp",EDGE,"E23.2.0.3"),sQuery(id+"F0.wireOp",EDGE,"E23.3.0.0"),sQuery(id+"F0.wireOp",EDGE,"E23.3.0.1"),sQuery(id+"F0.wireOp",EDGE,"E23.3.0.2"),sQuery(id+"F0.wireOp",EDGE,"E23.3.0.3"),sQuery(id+"F0.wireOp",EDGE,"E24.MirrorC"),sQuery(id+"F0.wireOp",EDGE,"E25.MirrorCS"),sQuery(id+"F0.wireOp",EDGE,"E26.MirrorC"),sQuery(id+"F0.wireOp",EDGE,"E27.MirrorCS"),sQuery(id+"F0.wireOp",EDGE,"E28.MirrorC"),sQuery(id+"F0.wireOp",EDGE,"E29.MirrorCS"),sQuery(id+"F0.wireOp",EDGE,"E30.MirrorCS"),sQuery(id+"F0.wireOp",EDGE,"E31.MirrorC"),sQuery(id+"F0.wireOp",EDGE,"E32.MirrorC"),sQuery(id+"F0.wireOp",EDGE,"E33.MirrorC"),sQuery(id+"F0.wireOp",EDGE,"E34.MirrorCS"),sQuery(id+"F0.wireOp",EDGE,"E35.MirrorCS"),sQuery(id+"F0.wireOp",EDGE,"E36.MirrorC"),sQuery(id+"F0.wireOp",EDGE,"E37.MirrorC"),sQuery(id+"F0.wireOp",EDGE,"E38.MirrorCS"),sQuery(id+"F0.wireOp",EDGE,"E39.MirrorCS"),sQuery(id+"F0.wireOp",EDGE,"E40.MirrorC"),sQuery(id+"F0.wireOp",EDGE,"E41.MirrorC"),sQuery(id+"F0.wireOp",EDGE,"E42.MirrorCS"),sQuery(id+"F0.wireOp",EDGE,"E43.MirrorCS"),sQuery(id+"F0.wireOp",EDGE,"E44.MirrorCS"),sQuery(id+"F0.wireOp",EDGE,"E45.MirrorCS"),sQuery(id+"F0.wireOp",EDGE,"E46.MirrorC"),sQuery(id+"F0.wireOp",EDGE,"E47.MirrorC"),sQuery(id+"F0.wireOp",EDGE,"E50"),sQuery(id+"F0.wireOp",EDGE,"E51"),sQuery(id+"F0.wireOp",EDGE,"E52"),sQuery(id+"F0.wireOp",EDGE,"E53"),sQuery(id+"F0.wireOp",EDGE,"E54"),sQuery(id+"F0.wireOp",EDGE,"E55"),sQuery(id+"F0.wireOp",EDGE,"E56"),sQuery(id+"F0.wireOp",EDGE,"E57"),sQuery(id+"F0.wireOp",EDGE,"E60.MirrorC"),sQuery(id+"F0.wireOp",EDGE,"E61.MirrorCS"),sQuery(id+"F0.wireOp",EDGE,"E62.MirrorCS"),sQuery(id+"F0.wireOp",EDGE,"E63.MirrorC"),sQuery(id+"F0.wireOp",EDGE,"E64.MirrorCS"),sQuery(id+"F0.wireOp",EDGE,"E65.MirrorC"),sQuery(id+"F0.wireOp",EDGE,"E66.MirrorCS"),sQuery(id+"F0.wireOp",EDGE,"E67.MirrorC")])],"isStart":false})});}
            var Q3;
            Q3=makeQuery(id+"F3.boolean.opBoolean","COPY",FACE,{"derivedFrom":makeQuery(id+"F3.opExtrude","SWEPT_FACE",FACE,{"disambiguationData":[OSD([sQuery(id+"F2.wireOp",EDGE,"E71.top")])]})});
            var Q4;
            Q4=makeQuery(id+"F3.boolean.opBoolean","COPY",FACE,{"derivedFrom":makeQuery(id+"F3.opExtrude","SWEPT_FACE",FACE,{"disambiguationData":[OSD([sQuery(id+"F2.wireOp",EDGE,"E71.right")])]})});
            var Q5;
            Q5=makeQuery(id+"F3.boolean.opBoolean","COPY",FACE,{"derivedFrom":makeQuery(id+"F3.opExtrude","SWEPT_FACE",FACE,{"disambiguationData":[OSD([sQuery(id+"F2.wireOp",EDGE,"E75")])]})});
            var Q6;
            {var subQ0=sQuery(id+"F0.wireOp",EDGE,"E0.top");var subQ1=sQuery(id+"F0.wireOp",EDGE,"E0.left");var subQ2=sQuery(id+"F0.wireOp",EDGE,"E0.right");Q6=makeQuery(id+"F3.boolean.opBoolean","SPLIT",FACE,{"disambiguationData":[TD([makeQuery(id+"F1.opExtrude","SWEPT_FACE",FACE,{"disambiguationData":[OSD([subQ0])]})])],"derivedFrom":makeQuery(id+"F1.opExtrude","CAP_FACE",FACE,{"disambiguationData":[OSD([sQuery(id+"F0.wireOp",EDGE,"E0.bottom"),subQ0,subQ1,subQ2,sQuery(id+"F0.wireOp",EDGE,"E7"),sQuery(id+"F0.wireOp",EDGE,"E8"),sQuery(id+"F0.wireOp",EDGE,"E9"),sQuery(id+"F0.wireOp",EDGE,"E10"),sQuery(id+"F0.wireOp",EDGE,"E12"),sQuery(id+"F0.wireOp",EDGE,"E13"),sQuery(id+"F0.wireOp",EDGE,"E14"),sQuery(id+"F0.wireOp",EDGE,"E15"),sQuery(id+"F0.wireOp",EDGE,"E17"),sQuery(id+"F0.wireOp",EDGE,"E18"),sQuery(id+"F0.wireOp",EDGE,"E19"),sQuery(id+"F0.wireOp",EDGE,"E20"),sQuery(id+"F0.wireOp",EDGE,"E22.1.0.0"),sQuery(id+"F0.wireOp",EDGE,"E22.1.0.1"),sQuery(id+"F0.wireOp",EDGE,"E22.1.0.2"),sQuery(id+"F0.wireOp",EDGE,"E22.1.0.3"),sQuery(id+"F0.wireOp",EDGE,"E22.2.0.0"),sQuery(id+"F0.wireOp",EDGE,"E22.2.0.1"),sQuery(id+"F0.wireOp",EDGE,"E22.2.0.2"),sQuery(id+"F0.wireOp",EDGE,"E22.2.0.3"),sQuery(id+"F0.wireOp",EDGE,"E22.3.0.0"),sQuery(id+"F0.wireOp",EDGE,"E22.3.0.1"),sQuery(id+"F0.wireOp",EDGE,"E22.3.0.2"),sQuery(id+"F0.wireOp",EDGE,"E22.3.0.3"),sQuery(id+"F0.wireOp",EDGE,"E23.1.0.0"),sQuery(id+"F0.wireOp",EDGE,"E23.1.0.1"),sQuery(id+"F0.wireOp",EDGE,"E23.1.0.2"),sQuery(id+"F0.wireOp",EDGE,"E23.1.0.3"),sQuery(id+"F0.wireOp",EDGE,"E23.2.0.0"),sQuery(id+"F0.wireOp",EDGE,"E23.2.0.1"),sQuery(id+"F0.wireOp",EDGE,"E23.2.0.2"),sQuery(id+"F0.wireOp",EDGE,"E23.2.0.3"),sQuery(id+"F0.wireOp",EDGE,"E23.3.0.0"),sQuery(id+"F0.wireOp",EDGE,"E23.3.0.1"),sQuery(id+"F0.wireOp",EDGE,"E23.3.0.2"),sQuery(id+"F0.wireOp",EDGE,"E23.3.0.3"),sQuery(id+"F0.wireOp",EDGE,"E24.MirrorC"),sQuery(id+"F0.wireOp",EDGE,"E25.MirrorCS"),sQuery(id+"F0.wireOp",EDGE,"E26.MirrorC"),sQuery(id+"F0.wireOp",EDGE,"E27.MirrorCS"),sQuery(id+"F0.wireOp",EDGE,"E28.MirrorC"),sQuery(id+"F0.wireOp",EDGE,"E29.MirrorCS"),sQuery(id+"F0.wireOp",EDGE,"E30.MirrorCS"),sQuery(id+"F0.wireOp",EDGE,"E31.MirrorC"),sQuery(id+"F0.wireOp",EDGE,"E32.MirrorC"),sQuery(id+"F0.wireOp",EDGE,"E33.MirrorC"),sQuery(id+"F0.wireOp",EDGE,"E34.MirrorCS"),sQuery(id+"F0.wireOp",EDGE,"E35.MirrorCS"),sQuery(id+"F0.wireOp",EDGE,"E36.MirrorC"),sQuery(id+"F0.wireOp",EDGE,"E37.MirrorC"),sQuery(id+"F0.wireOp",EDGE,"E38.MirrorCS"),sQuery(id+"F0.wireOp",EDGE,"E39.MirrorCS"),sQuery(id+"F0.wireOp",EDGE,"E40.MirrorC"),sQuery(id+"F0.wireOp",EDGE,"E41.MirrorC"),sQuery(id+"F0.wireOp",EDGE,"E42.MirrorCS"),sQuery(id+"F0.wireOp",EDGE,"E43.MirrorCS"),sQuery(id+"F0.wireOp",EDGE,"E44.MirrorCS"),sQuery(id+"F0.wireOp",EDGE,"E45.MirrorCS"),sQuery(id+"F0.wireOp",EDGE,"E46.MirrorC"),sQuery(id+"F0.wireOp",EDGE,"E47.MirrorC"),sQuery(id+"F0.wireOp",EDGE,"E50"),sQuery(id+"F0.wireOp",EDGE,"E51"),sQuery(id+"F0.wireOp",EDGE,"E52"),sQuery(id+"F0.wireOp",EDGE,"E53"),sQuery(id+"F0.wireOp",EDGE,"E54"),sQuery(id+"F0.wireOp",EDGE,"E55"),sQuery(id+"F0.wireOp",EDGE,"E56"),sQuery(id+"F0.wireOp",EDGE,"E57"),sQuery(id+"F0.wireOp",EDGE,"E60.MirrorC"),sQuery(id+"F0.wireOp",EDGE,"E61.MirrorCS"),sQuery(id+"F0.wireOp",EDGE,"E62.MirrorCS"),sQuery(id+"F0.wireOp",EDGE,"E63.MirrorC"),sQuery(id+"F0.wireOp",EDGE,"E64.MirrorCS"),sQuery(id+"F0.wireOp",EDGE,"E65.MirrorC"),sQuery(id+"F0.wireOp",EDGE,"E66.MirrorCS"),sQuery(id+"F0.wireOp",EDGE,"E67.MirrorC")])],"isStart":false})});}
            var Q7;
            Q7=makeQuery(id+"F1.opExtrude","SWEPT_FACE",FACE,{"disambiguationData":[OSD([sQuery(id+"F0.wireOp",EDGE,"E0.top")])]});
            fillet(context, id + "F6", {"entities" : qUnion([Q0, Q1, Q2, Q3, Q4, Q5, Q6, Q7]), "radius" : 1.27 * mm, "tangentPropagation" : true, "allowEdgeOverflow" : false});
        }
    });
